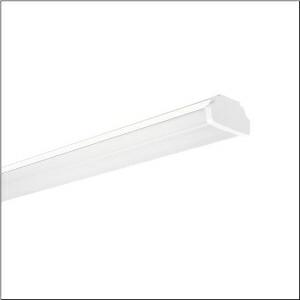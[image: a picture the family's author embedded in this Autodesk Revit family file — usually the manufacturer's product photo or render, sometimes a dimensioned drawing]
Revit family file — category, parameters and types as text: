
# Revit family: modario_r__31_gen_2_53bm812cv675c2_0c1f
name_source: partatom
category: Lighting Fixtures
units: mm (PartAtom-declared; Revit-internal decimal feet)

## family parameters
Cut with Voids When Loaded = No
Host = Face
Light Source = No
Part Type = Normal
Room Calculation Point = No
Round Connector Dimension = Use Diameter
Shared = No

## types (1)
- --- (1 x LED, 7670 lm, 42.1 W, 6500K)
    Apparent Load = 42 VA
    CIE Flux Codes = 47 80 95 93 100
    Color Rendering = 80
    Color Temperature = 6500K
    Default Elevation = 1800 mm
    Description = Modario® 31 Gen.2, luminaire insert, of sheet steel, coil coated, white, length: 1.495mm, width: 81mm, height: 82mm, 5x system unit, system units: 299mm, LED rated luminous flux: 7.670lm, light colour: 865, control gear: ON/OFF Multilumen, CLOi, with plug, 3-pole, with phase selection, mains connection: 220..240V, AC, 50/60Hz, start of lifetime: 42W, end of service life: 50W, through-wiring accessed according to module size, primary optical cover: cover, of PMMA, light emission: direct distribution, primary light characteristic: symmetric, protection rating (complete): IP20, protection rating (LED compartment): IP50, insulation class (complete): insulation class I (protective earthing), certification: CE, ENEC, VDE, UKCA, impact resistance: IK03, permissible ambient temperature for indoor applications: -35..+50°C, corresponds to IFS (International Featured Standards) requirements for safety and quality in the food industry, reducing of maximum allowable ambient temperature of 5°C with ceiling mounting, IP40 when using the optional accessory 5TP9018, packaging unit: 1 piece
    Height = 92 mm
    Lamp = 1 x LED
    Lamp Light Flux = 7670 lm
    Lamp Power = 42.1 W
    Lamp count = 1
    Length = 1495 mm
    Luminous efficacy = 182 lm/W
    Manufacturer = Siteco
    ModVariant = No
    Model = 53BM812CV675C2
    Mounting Place = Ceiling
    Mounting Type = Pendant
    Number of Poles = 1
    OnlyDefault = Yes
    Power Factor = 1
    Product Name = Modario® 31 Gen.2
    Product group = luminaire insert
    ProductGroupID = 902
    Protection Class = Protection class I
    Protection Degree = IP 20
    RLX_Detail_Level = 1
    RLX_Emergency_Light_Flux = 0 lm
    RLX_Emergency_Type = 0
    RLX_Emergency_Type_DB = No
    RlxData = <blob elided: 40025 chars, md5=564705e5>
    Socket = socket
    Standby Power = 0 W
    System Light Flux = 7670 lm
    System Power = 42 W
    Type Comments = factory setting: luminous flux: 100 % | (A | C | E) | 98 mA
    Type Image = l_1341886.jpg
    URL = http://relux.com
    VarID = @adj_034098
    Voltage = 0 V
    Weight = 0.00 kg
    Width = 81 mm

## geometry (parser evidence)
native form markers: Blend x4, Sweep x12
no freeform markers — native parametric forms only
